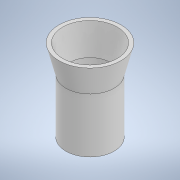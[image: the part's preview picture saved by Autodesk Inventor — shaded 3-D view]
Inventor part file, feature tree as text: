
AUTODESK INVENTOR PART (.ipt)
format: ipt  version: 2022 (Build 260153000, 153)  size: 119,808 bytes
history: native  units: mm
features: sketch x2, extrude x1, revolve x1
ambient origin geometry x8: Origin, YZ Plane, XZ Plane, XY Plane, X Axis, Y Axis, Z Axis, Center Point
bodies: Solid1 (feature_tree)
feature tree (4):
  extrude  "Extrusion1"  Depth=17.75mm
  revolve  "Revolution1"  [1 undecoded]
  sketch  "Sketch1"  dims[d0=15.0mm d1=17.75mm]
  sketch  "Sketch2"  dims[d2=20.0mm d3=0.0mm d4=10.0mm d5=10.0mm d7=90.0deg]
note: 1 required parameter value undecoded (feature->parameter linkage not recoverable at this tier; creation-order binding heuristic only, values carry confidence <= 0.55)
